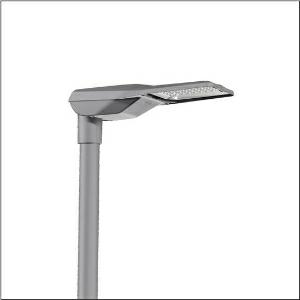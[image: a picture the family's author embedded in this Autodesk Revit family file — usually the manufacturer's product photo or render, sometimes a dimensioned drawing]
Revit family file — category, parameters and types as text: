
# Revit family: streetlight_sl_21_iq_mini___st0_5a_5xe2b41d08hb_2494
name_source: partatom
category: Lighting Fixtures
units: mm (PartAtom-declared; Revit-internal decimal feet)

## family parameters
Cut with Voids When Loaded = No
Host = Face
Light Source = No
Part Type = Normal
Room Calculation Point = No
Round Connector Dimension = Use Diameter
Shared = No

## types (1)
- --- (1 x LED, 9860 lm, 70.9 W, 4000K)
    Apparent Load = 71 VA
    CIE Flux Codes = 41 75 97 100 100
    Color Rendering = 70
    Color Temperature = 4000K
    Default Elevation = 1800 mm
    Description = Streetlight SL 21 iQ mini, mast luminaire, primary light control with lens, of PMMA, primary optical cover: cover, of toughened safety glass, transparent, light distribution: ST0.5a, light emission: direct distribution, primary light characteristic: asymmetric, installation type: post-top, side-entry, LED, High Power LED, rated luminous flux: 9.860lm, luminous efficacy: 139lm/W, light colour: 740, colour temperature: 4000K, control gear: iQ-Comfort, control: Auto-Match, Temp-Guard, Lumen-Switch, Night-Set, Smart-Wire, Light-Fading, Desk-Remote (wireless, voltage-free reading and setting of iQ features in the workshop via application-optimized NFC function/RFID function), optimised constant luminous flux control (CLO 2.0), pre-setting: linear dimming characteristic, mains connection: 220..240V, AC, 50/60Hz, start of lifetime: 71W, end of service life: 75W, reduction: 31W, luminaire housing, of diecast aluminium, powder-coated, SITECO metallic grey (DB 702S), corrosivity category C5 high according to DIN EN ISO 12944, please order mast flange separately, inclination adjustable: 0°, 5°, 10°, 15°, sealing non-destructively replaceable, multi-level sealing system, length: 628mm, width: 235mm, height: 110mm, mast flange for spigot size: 42mm (side-entry): 5XC10008XM4, 60/48mm (side-entry/post-top): 5XC10108XM2, 76/60mm (side-entry/post-top): 5XC10108XM1, mounting height: 4..8m, protection rating (complete): IP66, insulation class (complete): insulation class II (safety insulation), certification: CE, ENEC, ENEC+, VDE, impact resistance: IK10, permissible operating ambient temperature for outdoor applications: -40..+50°C, standard-compliant lighting for roads and squares, packaging unit: 1 piece

Light Distribution: ST0.5a
    Height = 110 mm
    Lamp = 1 x LED
    Lamp Light Flux = 9860 lm
    Lamp Power = 70.9 W
    Lamp count = 1
    Length = 625 mm
    Luminous efficacy = 139 lm/W
    Manufacturer = Siteco
    ModVariant = No
    Model = 5XE2B41D08HB
    Number of Poles = 1
    OnlyDefault = Yes
    Power Factor = 1
    Product Name = Streetlight SL 21 iQ mini | ST0.5a
    Product group = mast luminaire | pylon top
    ProductGroupID = 6100
    Protection Class = Protection class II
    Protection Degree = IP 66
    RLX_Detail_Level = 1
    RLX_Emergency_Light_Flux = 0 lm
    RLX_Emergency_Type = 0
    RLX_Emergency_Type_DB = No
    RlxData = <blob elided: 37277 chars, md5=5446a4c3>
    Socket = socket
    Standby Power = 0 W
    System Light Flux = 9860 lm
    System Power = 71 W
    Type Comments = factory setting: luminous flux: 100 % | dim-lin: 254 | 711 mA
    Type Image = l_1003519.jpg
    URL = http://relux.com
    VarID = @adj_158021
    Voltage = 0 V
    Weight = 0.00 kg
    Width = 234 mm

## geometry (parser evidence)
native form markers: Blend x4, Sweep x11
no freeform markers — native parametric forms only
